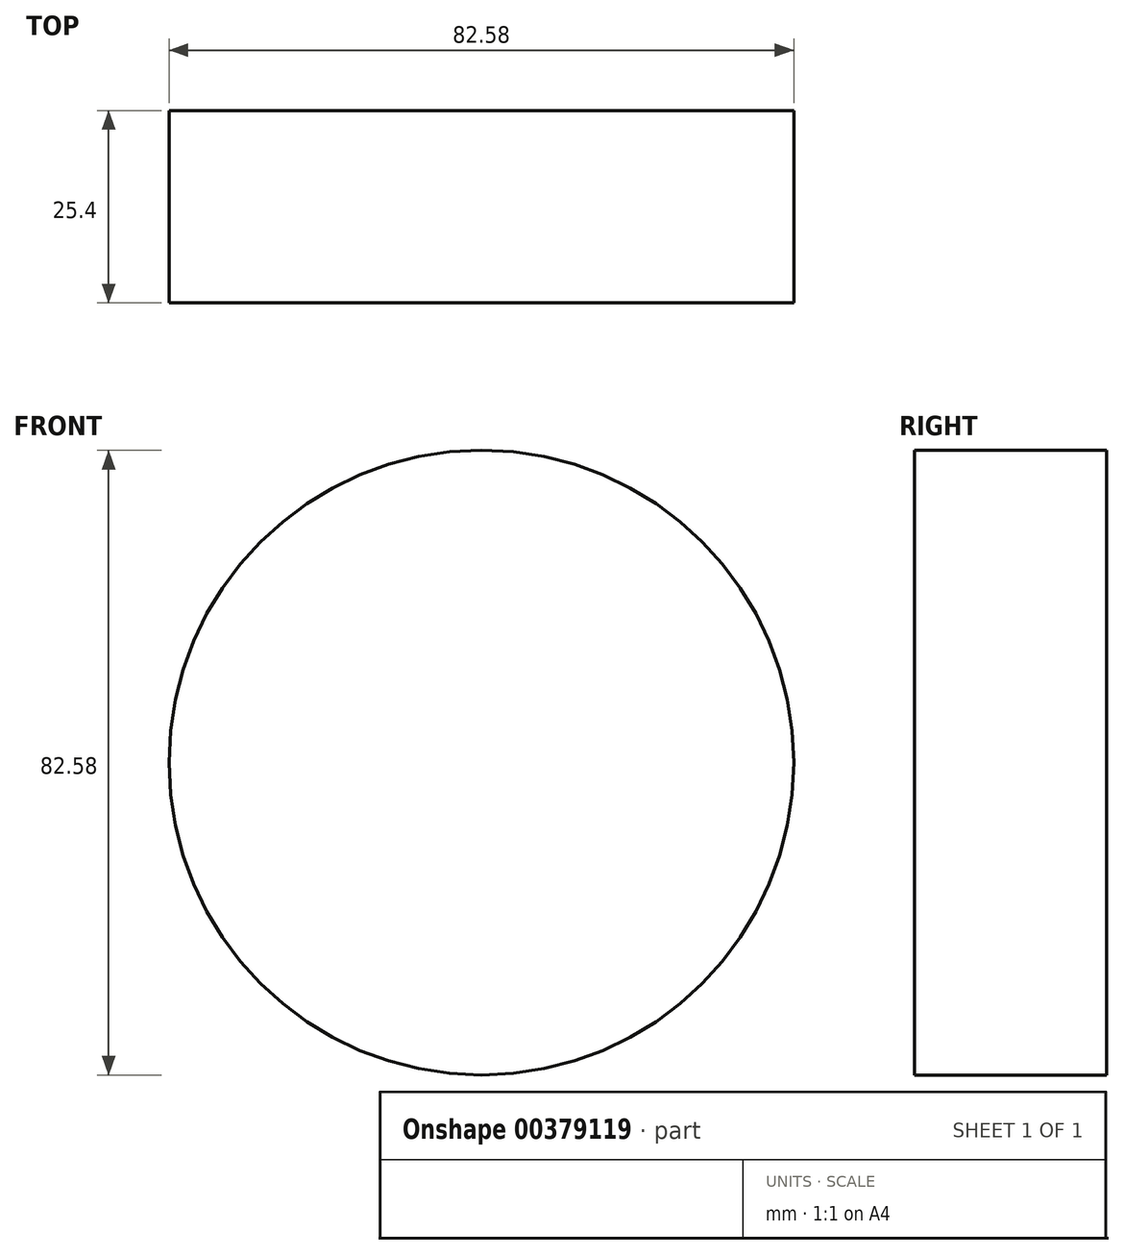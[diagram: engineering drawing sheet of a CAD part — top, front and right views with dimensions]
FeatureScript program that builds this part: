
annotation { "Feature Type Name" : "Feature", "Feature Type Description" : "" }
export const myFeature = defineFeature(function(context is Context, id is Id, definition is map)
    precondition{}
    {
        {
            var Q0;
            Q0=qCreatedBy(makeId("Front.planeOp"),FACE);
            var sketch = newSketch(context, id + "F0", { "sketchPlane" : qUnion([Q0])});
            skCircle(sketch, "E0", {"center": v(0, 0) * mm, "radius": 41.3 * mm});
            skSolve(sketch);
        }
        {
            var Q0;
            Q0 = qSketchRegion(id + "F0", true);
            extrude(context, id + "F1", {"entities" : qUnion([Q0]), "depth" : 25.4 * mm});
        }
    });
